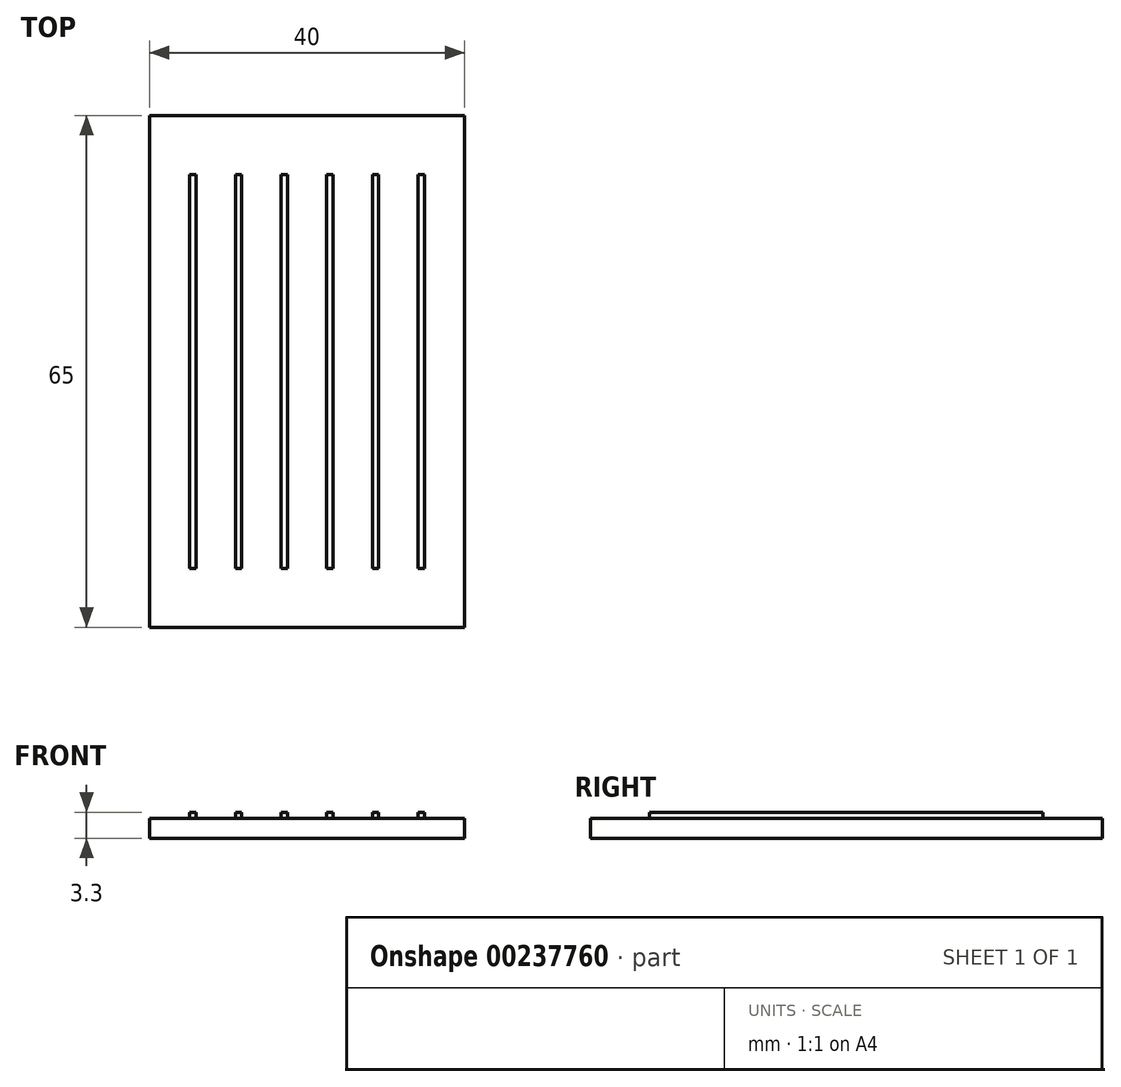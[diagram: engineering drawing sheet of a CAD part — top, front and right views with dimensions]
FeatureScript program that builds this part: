
annotation { "Feature Type Name" : "Feature", "Feature Type Description" : "" }
export const myFeature = defineFeature(function(context is Context, id is Id, definition is map)
    precondition{}
    {
        {
            var Q0;
            Q0=qCreatedBy(makeId("Top.planeOp"),FACE);
            var sketch = newSketch(context, id + "F0", { "sketchPlane" : qUnion([Q0])});
            skLineSegment(sketch, "E0.bottom", {"start": v(-20, 32.5) * mm, "end": v(20, 32.5) * mm});
            skLineSegment(sketch, "E0.top", {"start": v(-20, -32.5) * mm, "end": v(20, -32.5) * mm});
            skLineSegment(sketch, "E0.left", {"start": v(-20, 32.5) * mm, "end": v(-20, -32.5) * mm});
            skLineSegment(sketch, "E0.right", {"start": v(20, 32.5) * mm, "end": v(20, -32.5) * mm});
            skPoint(sketch, "E0.middle", {"position": v(0, 0) * mm});
            skLineSegment(sketch, "E1.bottom", {"start": v(-14.9, 25) * mm, "end": v(-14.1, 25) * mm});
            skLineSegment(sketch, "E1.top", {"start": v(-14.9, -25) * mm, "end": v(-14.1, -25) * mm});
            skLineSegment(sketch, "E1.left", {"start": v(-14.9, 25) * mm, "end": v(-14.9, -25) * mm});
            skLineSegment(sketch, "E1.right", {"start": v(-14.1, 25) * mm, "end": v(-14.1, -25) * mm});
            skLineSegment(sketch, "E2.bottom", {"start": v(-9.1, 25) * mm, "end": v(-8.3, 25) * mm});
            skLineSegment(sketch, "E2.top", {"start": v(-9.1, -25) * mm, "end": v(-8.3, -25) * mm});
            skLineSegment(sketch, "E2.left", {"start": v(-9.1, 25) * mm, "end": v(-9.1, -25) * mm});
            skLineSegment(sketch, "E2.right", {"start": v(-8.3, 25) * mm, "end": v(-8.3, -25) * mm});
            skLineSegment(sketch, "E3.bottom", {"start": v(-3.3, 25) * mm, "end": v(-2.5, 25) * mm});
            skLineSegment(sketch, "E3.top", {"start": v(-3.3, -25) * mm, "end": v(-2.5, -25) * mm});
            skLineSegment(sketch, "E3.left", {"start": v(-3.3, 25) * mm, "end": v(-3.3, -25) * mm});
            skLineSegment(sketch, "E3.right", {"start": v(-2.5, 25) * mm, "end": v(-2.5, -25) * mm});
            skLineSegment(sketch, "E4", {"start": v(0, 32.5) * mm, "end": v(0, -32.5) * mm, "construction": true});
            skLineSegment(sketch, "E5.MirrorCS", {"start": v(2.5, 25) * mm, "end": v(2.5, -25) * mm});
            skLineSegment(sketch, "E6.MirrorCS", {"start": v(3.3, 25) * mm, "end": v(3.3, -25) * mm});
            skLineSegment(sketch, "E7.MirrorCS", {"start": v(3.3, 25) * mm, "end": v(2.5, 25) * mm});
            skLineSegment(sketch, "E8.MirrorCS", {"start": v(9.1, 25) * mm, "end": v(8.3, 25) * mm});
            skLineSegment(sketch, "E9.MirrorCS", {"start": v(8.3, 25) * mm, "end": v(8.3, -25) * mm});
            skLineSegment(sketch, "E10.MirrorCS", {"start": v(9.1, 25) * mm, "end": v(9.1, -25) * mm});
            skLineSegment(sketch, "E11.MirrorCS", {"start": v(14.9, 25) * mm, "end": v(14.1, 25) * mm});
            skLineSegment(sketch, "E12.MirrorCS", {"start": v(14.1, 25) * mm, "end": v(14.1, -25) * mm});
            skLineSegment(sketch, "E13.MirrorCS", {"start": v(14.9, 25) * mm, "end": v(14.9, -25) * mm});
            skLineSegment(sketch, "E14.MirrorCS", {"start": v(14.9, -25) * mm, "end": v(14.1, -25) * mm});
            skLineSegment(sketch, "E15.MirrorCS", {"start": v(9.1, -25) * mm, "end": v(8.3, -25) * mm});
            skLineSegment(sketch, "E16.MirrorCS", {"start": v(3.3, -25) * mm, "end": v(2.5, -25) * mm});
            skSolve(sketch);
        }
        {
            var Q0;
            Q0=makeQuery(id+"F0.imprint","IMPRINT",FACE,{"disambiguationData":[TD([[makeQuery(id+"F0.imprint","IMPRINT",EDGE,{"derivedFrom":sQuery(id+"F0.wireOp",EDGE,"E0.bottom")}),-1.0]])]});
            var Q1;
            Q1=makeQuery(id+"F0.imprint","IMPRINT",FACE,{"disambiguationData":[TD([[makeQuery(id+"F0.imprint","IMPRINT",EDGE,{"derivedFrom":sQuery(id+"F0.wireOp",EDGE,"E11.MirrorCS")}),1.0]])]});
            var Q2;
            Q2=makeQuery(id+"F0.imprint","IMPRINT",FACE,{"disambiguationData":[TD([[makeQuery(id+"F0.imprint","IMPRINT",EDGE,{"derivedFrom":sQuery(id+"F0.wireOp",EDGE,"E8.MirrorCS")}),1.0]])]});
            var Q3;
            Q3=makeQuery(id+"F0.imprint","IMPRINT",FACE,{"disambiguationData":[TD([[makeQuery(id+"F0.imprint","IMPRINT",EDGE,{"derivedFrom":sQuery(id+"F0.wireOp",EDGE,"E5.MirrorCS")}),1.0]])]});
            var Q4;
            Q4=makeQuery(id+"F0.imprint","IMPRINT",FACE,{"disambiguationData":[TD([[makeQuery(id+"F0.imprint","IMPRINT",EDGE,{"derivedFrom":sQuery(id+"F0.wireOp",EDGE,"E3.bottom")}),-1.0]])]});
            var Q5;
            Q5=makeQuery(id+"F0.imprint","IMPRINT",FACE,{"disambiguationData":[TD([[makeQuery(id+"F0.imprint","IMPRINT",EDGE,{"derivedFrom":sQuery(id+"F0.wireOp",EDGE,"E2.bottom")}),-1.0]])]});
            var Q6;
            Q6=makeQuery(id+"F0.imprint","IMPRINT",FACE,{"disambiguationData":[TD([[makeQuery(id+"F0.imprint","IMPRINT",EDGE,{"derivedFrom":sQuery(id+"F0.wireOp",EDGE,"E1.bottom")}),-1.0]])]});
            extrude(context, id + "F1", {"entities" : qUnion([Q0, Q1, Q2, Q3, Q4, Q5, Q6]), "oppositeDirection" : true, "depth" : 2.5 * mm});
        }
        {
            var Q0;
            Q0=makeQuery(id+"F0.imprint","IMPRINT",FACE,{"disambiguationData":[TD([[makeQuery(id+"F0.imprint","IMPRINT",EDGE,{"derivedFrom":sQuery(id+"F0.wireOp",EDGE,"E11.MirrorCS")}),1.0]])]});
            var Q1;
            Q1=makeQuery(id+"F0.imprint","IMPRINT",FACE,{"disambiguationData":[TD([[makeQuery(id+"F0.imprint","IMPRINT",EDGE,{"derivedFrom":sQuery(id+"F0.wireOp",EDGE,"E8.MirrorCS")}),1.0]])]});
            var Q2;
            Q2=makeQuery(id+"F0.imprint","IMPRINT",FACE,{"disambiguationData":[TD([[makeQuery(id+"F0.imprint","IMPRINT",EDGE,{"derivedFrom":sQuery(id+"F0.wireOp",EDGE,"E5.MirrorCS")}),1.0]])]});
            var Q3;
            Q3=makeQuery(id+"F0.imprint","IMPRINT",FACE,{"disambiguationData":[TD([[makeQuery(id+"F0.imprint","IMPRINT",EDGE,{"derivedFrom":sQuery(id+"F0.wireOp",EDGE,"E3.bottom")}),-1.0]])]});
            var Q4;
            Q4=makeQuery(id+"F0.imprint","IMPRINT",FACE,{"disambiguationData":[TD([[makeQuery(id+"F0.imprint","IMPRINT",EDGE,{"derivedFrom":sQuery(id+"F0.wireOp",EDGE,"E2.bottom")}),-1.0]])]});
            var Q5;
            Q5=makeQuery(id+"F0.imprint","IMPRINT",FACE,{"disambiguationData":[TD([[makeQuery(id+"F0.imprint","IMPRINT",EDGE,{"derivedFrom":sQuery(id+"F0.wireOp",EDGE,"E1.bottom")}),-1.0]])]});
            extrude(context, id + "F2", {"entities" : qUnion([Q0, Q1, Q2, Q3, Q4, Q5]), "operationType" : NewBodyOperationType.ADD, "depth" : 0.8 * mm});
        }
    });
